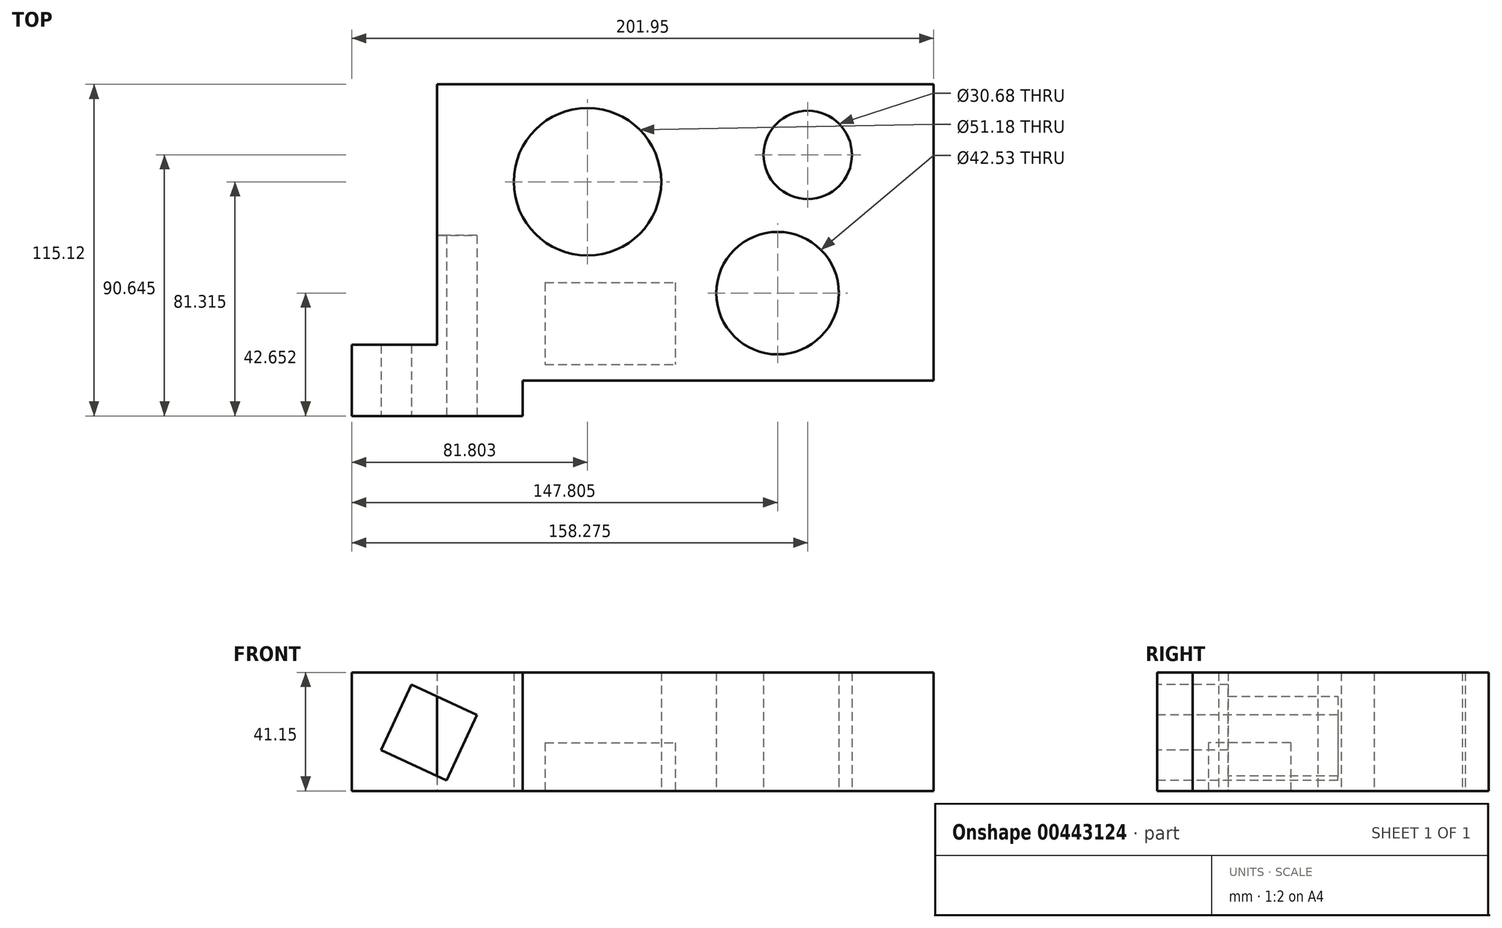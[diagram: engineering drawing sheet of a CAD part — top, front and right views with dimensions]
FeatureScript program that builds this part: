
annotation { "Feature Type Name" : "Feature", "Feature Type Description" : "" }
export const myFeature = defineFeature(function(context is Context, id is Id, definition is map)
    precondition{}
    {
        {
            var Q0;
            Q0=qCreatedBy(makeId("Top.planeOp"),FACE);
            var sketch = newSketch(context, id + "F0", { "sketchPlane" : qUnion([Q0])});
            skLineSegment(sketch, "E0.bottom", {"start": v(86.15, 51.38) * mm, "end": v(-86.15, 51.38) * mm});
            skLineSegment(sketch, "E0.top", {"start": v(86.15, -51.38) * mm, "end": v(-86.15, -51.38) * mm});
            skLineSegment(sketch, "E0.left", {"start": v(86.15, 51.38) * mm, "end": v(86.15, -51.38) * mm});
            skLineSegment(sketch, "E0.right", {"start": v(-86.15, 51.38) * mm, "end": v(-86.15, -51.38) * mm});
            skPoint(sketch, "E0.middle", {"position": v(0, 0) * mm});
            skCircle(sketch, "E1", {"center": v(-34, 17.57) * mm, "radius": 25.59 * mm});
            skCircle(sketch, "E2", {"center": v(42.47, 26.9) * mm, "radius": 15.34 * mm});
            skCircle(sketch, "E3", {"center": v(32, -21.09) * mm, "radius": 21.27 * mm});
            skLineSegment(sketch, "E4.bottom", {"start": v(-56.5, -63.74) * mm, "end": v(-115.8, -63.74) * mm});
            skLineSegment(sketch, "E4.top", {"start": v(-56.5, -39.03) * mm, "end": v(-115.8, -39.03) * mm});
            skLineSegment(sketch, "E4.left", {"start": v(-56.5, -63.74) * mm, "end": v(-56.5, -39.03) * mm});
            skLineSegment(sketch, "E4.right", {"start": v(-115.8, -63.74) * mm, "end": v(-115.8, -39.03) * mm});
            skPoint(sketch, "E4.middle", {"position": v(-86.15, -51.38) * mm});
            skSolve(sketch);
        }
        {
            var Q0;
            Q0 = qSketchRegion(id + "F0", true);
            extrude(context, id + "F1", {"entities" : qUnion([Q0]), "depth" : 41.15 * mm});
        }
        {
            var Q0;
            Q0=makeQuery(id+"F1.opExtrude","SWEPT_FACE",FACE,{"disambiguationData":[OSD([sQuery(id+"F0.wireOp",EDGE,"E4.bottom")])]});
            var sketch = newSketch(context, id + "F2", { "sketchPlane" : qUnion([Q0])});
            skCircle(sketch, "E5.cCircle", {"center": v(-88.98, 20.27) * mm, "radius": 12.55 * mm, "construction": true});
            skLineSegment(sketch, "E5.0", {"start": v(-72.3, 26.36) * mm, "end": v(-82.88, 3.6) * mm});
            skLineSegment(sketch, "E5.1", {"start": v(-82.88, 3.6) * mm, "end": v(-105.65, 14.17) * mm});
            skLineSegment(sketch, "E5.2", {"start": v(-105.65, 14.17) * mm, "end": v(-95.07, 36.94) * mm});
            skLineSegment(sketch, "E5.3", {"start": v(-95.07, 36.94) * mm, "end": v(-72.3, 26.36) * mm});
            skPoint(sketch, "E5.0.midPoint", {"position": v(-77.6, 14.98) * mm});
            skSolve(sketch);
        }
        {
            var Q0;
            Q0 = qSketchRegion(id + "F2", true);
            extrude(context, id + "F3", {"entities" : qUnion([Q0]), "operationType" : NewBodyOperationType.REMOVE, "oppositeDirection" : true, "depth" : 62.74 * mm});
        }
        {
            var Q0;
            Q0=qCreatedBy(makeId("Top.planeOp"),FACE);
            var sketch = newSketch(context, id + "F4", { "sketchPlane" : qUnion([Q0])});
            skLineSegment(sketch, "E6.bottom", {"start": v(-48.75, -17.41) * mm, "end": v(-3.58, -17.41) * mm});
            skLineSegment(sketch, "E6.top", {"start": v(-48.75, -45.92) * mm, "end": v(-3.58, -45.92) * mm});
            skLineSegment(sketch, "E6.left", {"start": v(-48.75, -17.41) * mm, "end": v(-48.75, -45.92) * mm});
            skLineSegment(sketch, "E6.right", {"start": v(-3.58, -17.41) * mm, "end": v(-3.58, -45.92) * mm});
            skSolve(sketch);
        }
        {
            var Q0;
            Q0 = qSketchRegion(id + "F4", true);
            extrude(context, id + "F5", {"entities" : qUnion([Q0]), "operationType" : NewBodyOperationType.REMOVE, "depth" : 16.76 * mm});
        }
    });
